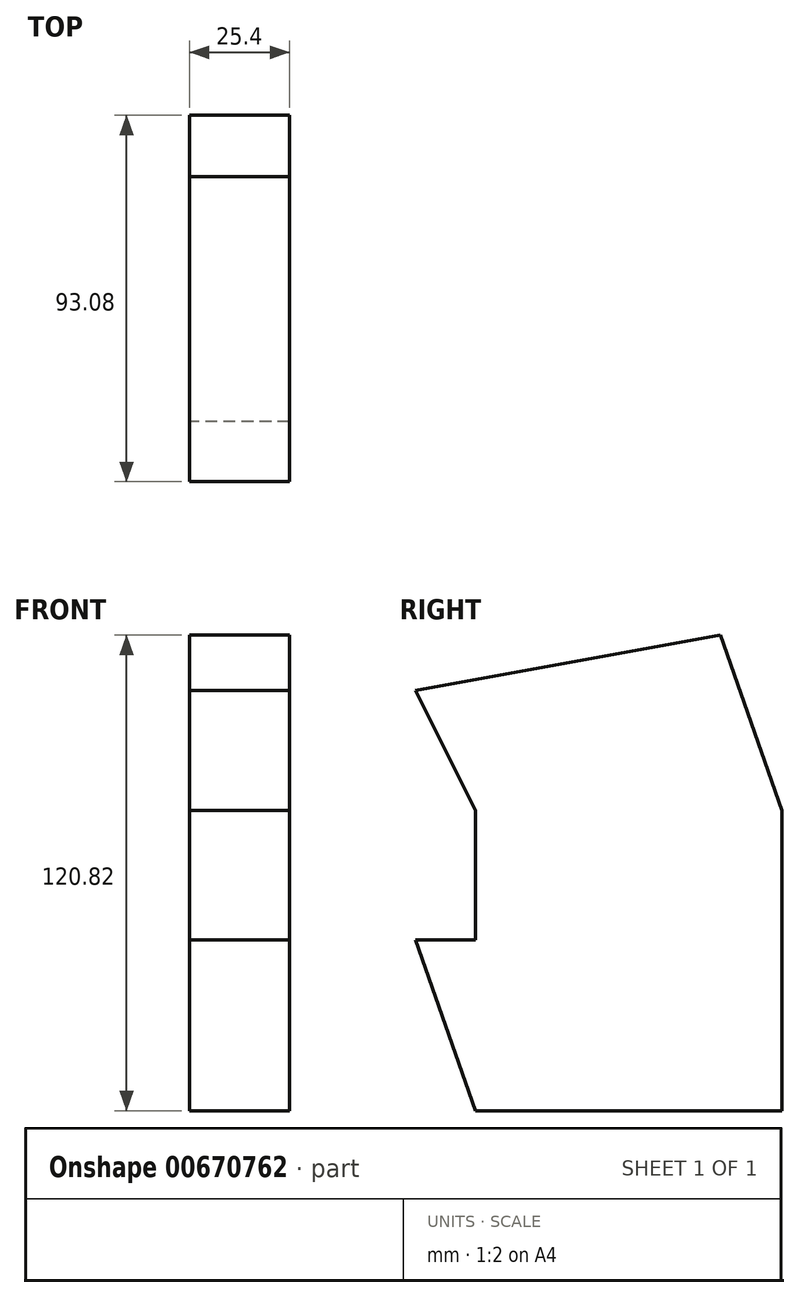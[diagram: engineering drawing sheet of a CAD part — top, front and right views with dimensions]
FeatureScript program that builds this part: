
annotation { "Feature Type Name" : "Feature", "Feature Type Description" : "" }
export const myFeature = defineFeature(function(context is Context, id is Id, definition is map)
    precondition{}
    {
        {
            var Q0;
            Q0=qCreatedBy(makeId("Right.planeOp"),FACE);
            var sketch = newSketch(context, id + "F0", { "sketchPlane" : qUnion([Q0])});
            skLineSegment(sketch, "E0", {"start": v(0, 0) * mm, "end": v(77.87, 0) * mm});
            skLineSegment(sketch, "E1", {"start": v(77.87, 0) * mm, "end": v(77.87, 76.24) * mm});
            skLineSegment(sketch, "E2", {"start": v(77.87, 76.24) * mm, "end": v(0, 76.24) * mm});
            skLineSegment(sketch, "E3", {"start": v(0, 76.24) * mm, "end": v(0, 0) * mm});
            skLineSegment(sketch, "E4", {"start": v(0, 0) * mm, "end": v(-15.2, 43.44) * mm});
            skLineSegment(sketch, "E5", {"start": v(-15.2, 43.44) * mm, "end": v(-15.2, 106.73) * mm});
            skLineSegment(sketch, "E6", {"start": v(-15.2, 106.73) * mm, "end": v(0, 76.24) * mm});
            skLineSegment(sketch, "E7", {"start": v(77.87, 76.24) * mm, "end": v(62.26, 120.82) * mm});
            skLineSegment(sketch, "E8", {"start": v(62.26, 120.82) * mm, "end": v(-15.2, 106.73) * mm});
            skLineSegment(sketch, "E9", {"start": v(-15.2, 43.44) * mm, "end": v(62.26, 43.44) * mm});
            skLineSegment(sketch, "E10", {"start": v(62.26, 43.44) * mm, "end": v(77.87, 0) * mm});
            skLineSegment(sketch, "E11", {"start": v(62.26, 43.44) * mm, "end": v(62.26, 120.82) * mm});
            skSolve(sketch);
        }
        {
            var Q0;
            {var subQ0=sQuery(id+"F0.wireOp",EDGE,"E7");Q0=makeQuery(id+"F0.imprint","IMPRINT",FACE,{"disambiguationData":[TD([[makeQuery(id+"F0.imprint","IMPRINT",EDGE,{"derivedFrom":subQ0}),1.0]])]});}
            var Q1;
            {var subQ0=sQuery(id+"F0.wireOp",EDGE,"E4");Q1=makeQuery(id+"F0.imprint","IMPRINT",FACE,{"disambiguationData":[TD([[makeQuery(id+"F0.imprint","IMPRINT",EDGE,{"derivedFrom":subQ0}),-1.0]])]});}
            var Q2;
            {var subQ0=sQuery(id+"F0.wireOp",EDGE,"E0");Q2=makeQuery(id+"F0.imprint","IMPRINT",FACE,{"disambiguationData":[TD([[makeQuery(id+"F0.imprint","IMPRINT",EDGE,{"derivedFrom":subQ0}),1.0]])]});}
            var Q3;
            {var subQ0=sQuery(id+"F0.wireOp",EDGE,"E1");Q3=makeQuery(id+"F0.imprint","IMPRINT",FACE,{"disambiguationData":[TD([[makeQuery(id+"F0.imprint","IMPRINT",EDGE,{"derivedFrom":subQ0}),1.0]])]});}
            var Q4;
            {var subQ0=sQuery(id+"F0.wireOp",EDGE,"E6");Q4=makeQuery(id+"F0.imprint","IMPRINT",FACE,{"disambiguationData":[TD([[makeQuery(id+"F0.imprint","IMPRINT",EDGE,{"derivedFrom":subQ0}),1.0]])]});}
            var Q5;
            {var subQ1=sQuery(id+"F0.wireOp",EDGE,"E2");var subQ3=sQuery(id+"F0.wireOp",EDGE,"E11");var subQ4=makeQuery(id+"F0.imprint","INTERSECT",VERTEX,{"derivedFrom":[subQ1,subQ3]});Q5=makeQuery(id+"F0.imprint","IMPRINT",FACE,{"disambiguationData":[TD([[makeQuery(id+"F0.imprint","IMPRINT",EDGE,{"disambiguationData":[TD([[subQ4,-1.0]])],"derivedFrom":subQ1}),1.0]])]});}
            extrude(context, id + "F1", {"entities" : qUnion([Q0, Q1, Q2, Q3, Q4, Q5]), "depth" : 25.4 * mm, "offsetDistance" : 25.4 * mm});
        }
    });
